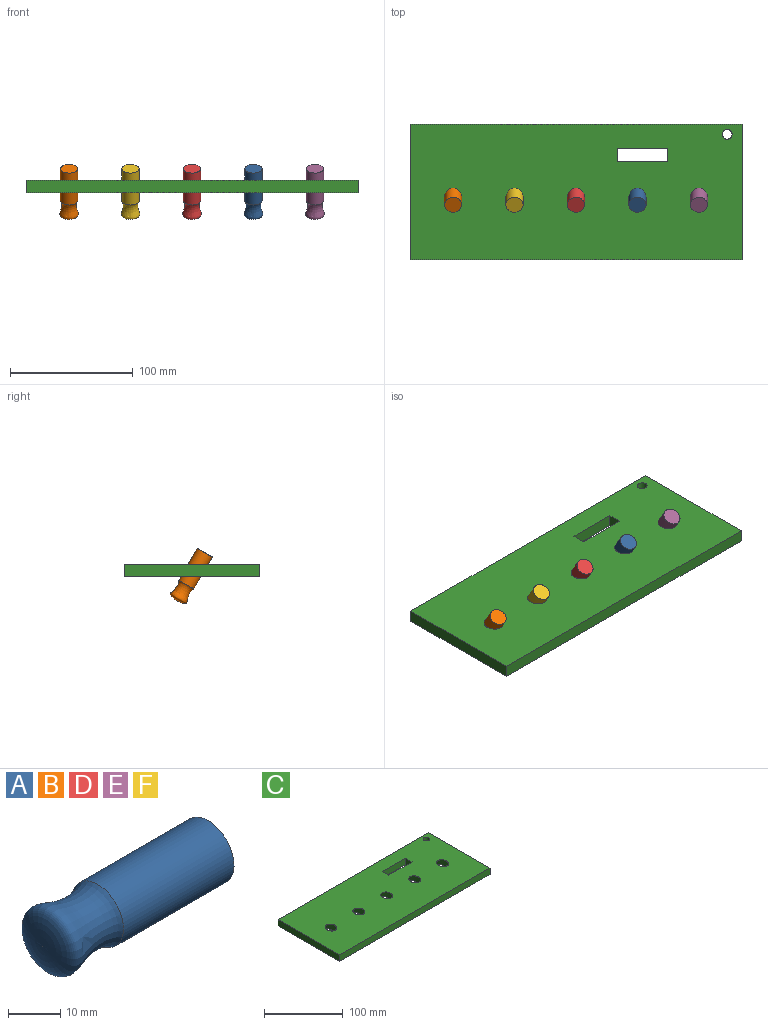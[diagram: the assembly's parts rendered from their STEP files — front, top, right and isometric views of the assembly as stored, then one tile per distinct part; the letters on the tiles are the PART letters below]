
ASSEMBLY  parts=6 mates=1
PART A: 3 faces, bbox 45x15x15 mm
  f0: revolved ~15.02x15.02mm, area 742.3mm2, adj f2
  f1: plane 14x14mm, normal (1,0,0), area 153.9mm2, adj f2
  f2: cylinder r=7mm len=30mm, axis (-1,0,0), area 1319.5mm2, adj f0,f1
PART B: same geometry as A
PART C: 17 faces, bbox 270x110x24 mm
  f0: plane 270x10mm, normal (0,1,0), area 2700mm2, adj f1,f8,f9,f10
  f1: plane 110x10mm, normal (-1,0,0), area 1100mm2, adj f0,f2,f9,f10
  f2: plane 270x10mm, normal (0,-1,0), area 2700mm2, adj f1,f8,f9,f10
  f3: plane 41.26x10mm, normal (0,-1,0), area 412.6mm2, adj f4,f7,f9,f10
  f4: plane 11.28x10mm, normal (-1,0,0), area 112.8mm2, adj f3,f5,f9,f10
  f5: plane 41.26x10mm, normal (0,1,0), area 412.6mm2, adj f4,f7,f9,f10
  f6: cylinder r=4mm len=8mm, axis (0,0,-1), area 175.9mm2, adj f9,f16
  f7: plane 11.28x10mm, normal (1,0,0), area 112.8mm2, adj f3,f5,f9,f10
  f8: plane 110x10mm, normal (1,0,0), area 1100mm2, adj f0,f2,f9,f10
  f9: plane 270x110mm, normal (0,0,1), area 28295.4mm2, adj f0,f1,f2,f3,f4,f5,f6,f7
  f10: plane 270x110mm, normal (0,0,-1), area 28191.7mm2, adj f0,f1,f2,f3,f4,f5,f7,f8
  f11: cylinder r=7mm len=24.05mm, axis (0,-0.5,0.87), area 507.9mm2, adj f9,f10
  f12: cylinder r=7mm len=24.05mm, axis (0,-0.5,0.87), area 507.9mm2, adj f9,f10
  f13: cylinder r=7mm len=24.05mm, axis (0,-0.5,0.87), area 507.9mm2, adj f9,f10
  f14: cylinder r=7mm len=24.05mm, axis (0,-0.5,0.87), area 507.9mm2, adj f9,f10
  f15: cylinder r=7mm len=24.05mm, axis (0,-0.5,0.87), area 507.9mm2, adj f9,f10
  f16: cone r=7mm half-angle=45deg, axis (0,0,-1), area 146.6mm2, adj f6,f10
PART D: same geometry as A
PART E: same geometry as A
PART F: same geometry as A
PLACE A rot(axis=(0.25,-0.94,-0.25),93.8deg) t=(60.32,-58.84,-3.91)mm
PLACE B rot(axis=(0.25,-0.94,-0.25),93.8deg) t=(-89.68,-58.84,-3.91)mm
PLACE C t=(10.32,-70.96,15.74)mm
PLACE D rot(axis=(0.25,-0.94,-0.25),93.8deg) t=(10.32,-58.84,-3.91)mm
PLACE E rot(axis=(0.25,-0.94,-0.25),93.8deg) t=(110.32,-58.84,-3.91)mm
PLACE F rot(axis=(0.25,-0.94,-0.25),93.8deg) t=(-39.68,-58.84,-3.91)mm
MATE slider E.f2 <-> C.f15  axis (0,-0.5,0.87) through (110.32,-81.34,35.06)mm
